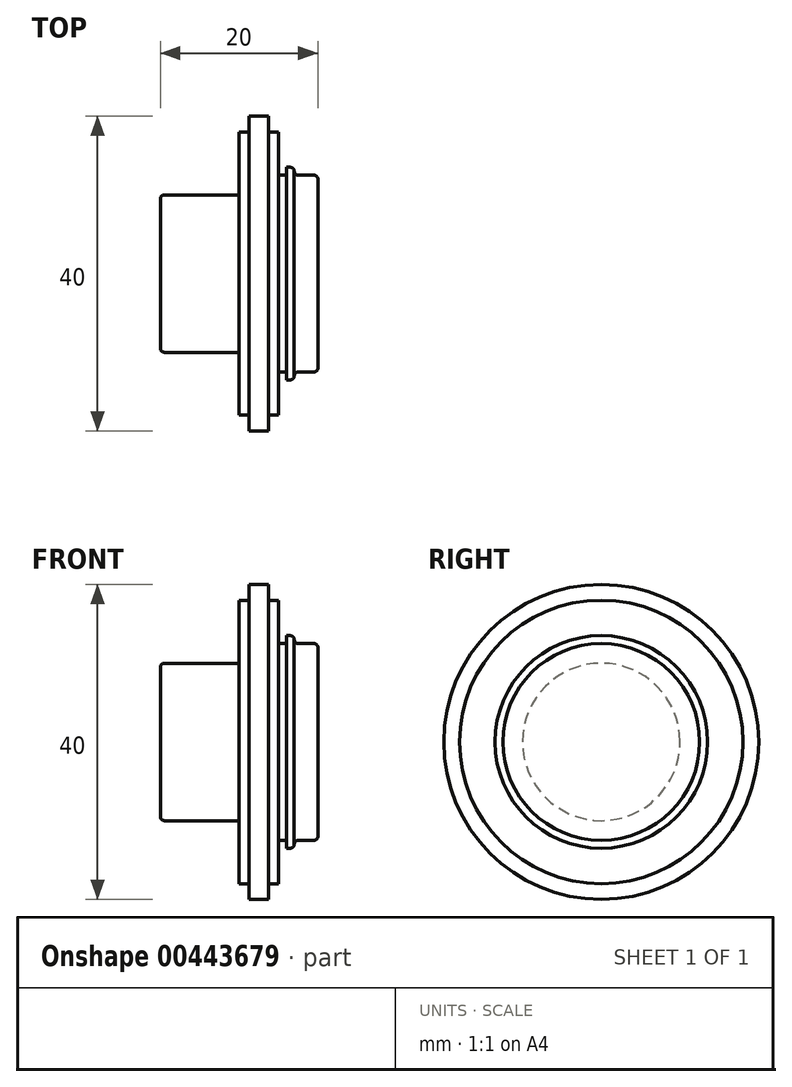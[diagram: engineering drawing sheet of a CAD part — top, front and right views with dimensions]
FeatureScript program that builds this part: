
annotation { "Feature Type Name" : "Feature", "Feature Type Description" : "" }
export const myFeature = defineFeature(function(context is Context, id is Id, definition is map)
    precondition{}
    {
        {
            var Q0;
            Q0=qCreatedBy(makeId("Front.planeOp"),FACE);
            var sketch = newSketch(context, id + "F0", { "sketchPlane" : qUnion([Q0])});
            skLineSegment(sketch, "E0", {"start": v(0, 0) * mm, "end": v(-20, 0) * mm});
            skLineSegment(sketch, "E1", {"start": v(-20, 0) * mm, "end": v(-20, 10) * mm});
            skLineSegment(sketch, "E2", {"start": v(-20, 10) * mm, "end": v(-10, 10) * mm});
            skLineSegment(sketch, "E3", {"start": v(-10, 10) * mm, "end": v(-10, 18) * mm});
            skLineSegment(sketch, "E4", {"start": v(-10, 18) * mm, "end": v(-8.75, 18) * mm});
            skLineSegment(sketch, "E5", {"start": v(-8.75, 18) * mm, "end": v(-8.75, 20) * mm});
            skLineSegment(sketch, "E6", {"start": v(-8.75, 20) * mm, "end": v(-6.25, 20) * mm});
            skLineSegment(sketch, "E7", {"start": v(-6.25, 20) * mm, "end": v(-6.25, 18) * mm});
            skLineSegment(sketch, "E8", {"start": v(-6.25, 18) * mm, "end": v(-5, 18) * mm});
            skLineSegment(sketch, "E9", {"start": v(-5, 18) * mm, "end": v(-5, 12.5) * mm});
            skLineSegment(sketch, "E10", {"start": v(-5, 12.5) * mm, "end": v(-4, 12.5) * mm});
            skLineSegment(sketch, "E11", {"start": v(-4, 12.5) * mm, "end": v(-4, 13.5) * mm});
            skLineSegment(sketch, "E12", {"start": v(-4, 13.5) * mm, "end": v(-3, 13.5) * mm});
            skLineSegment(sketch, "E13", {"start": v(-3, 13.5) * mm, "end": v(-3, 12.5) * mm});
            skLineSegment(sketch, "E14", {"start": v(-3, 12.5) * mm, "end": v(0, 12.5) * mm});
            skLineSegment(sketch, "E15", {"start": v(0, 12.5) * mm, "end": v(0, 0) * mm});
            skSolve(sketch);
        }
        {
            var Q0;
            Q0=makeQuery(id+"F0.imprint","IMPRINT",FACE,{"disambiguationData":[TD([[makeQuery(id+"F0.imprint","IMPRINT",EDGE,{"derivedFrom":sQuery(id+"F0.wireOp",EDGE,"E0")}),-1.0]])]});
            var Q1;
            Q1=sQuery(id+"F0.wireOp",EDGE,"E0");
            revolve(context, id + "F1", {"entities" : qUnion([Q0]), "axis" : qUnion([Q1]), "revolveType" : RevolveType.FULL});
        }
        {
            var Q0;
            Q0=makeQuery(id+"F1.opRevolve","SWEPT_EDGE",EDGE,{"disambiguationData":[OSD([sQuery(id+"F0.wireOp",EDGE,"E1"),sQuery(id+"F0.wireOp",EDGE,"E2")])]});
            var Q1;
            Q1=makeQuery(id+"F1.opRevolve","SWEPT_EDGE",EDGE,{"disambiguationData":[OSD([sQuery(id+"F0.wireOp",EDGE,"E12"),sQuery(id+"F0.wireOp",EDGE,"E13")])]});
            var Q2;
            Q2=makeQuery(id+"F1.opRevolve","SWEPT_FACE",FACE,{"disambiguationData":[OSD([sQuery(id+"F0.wireOp",EDGE,"E14")])]});
            fillet(context, id + "F2", {"entities" : qUnion([Q0, Q1, Q2]), "radius" : 0.5 * mm, "tangentPropagation" : true, "allowEdgeOverflow" : false});
        }
    });
